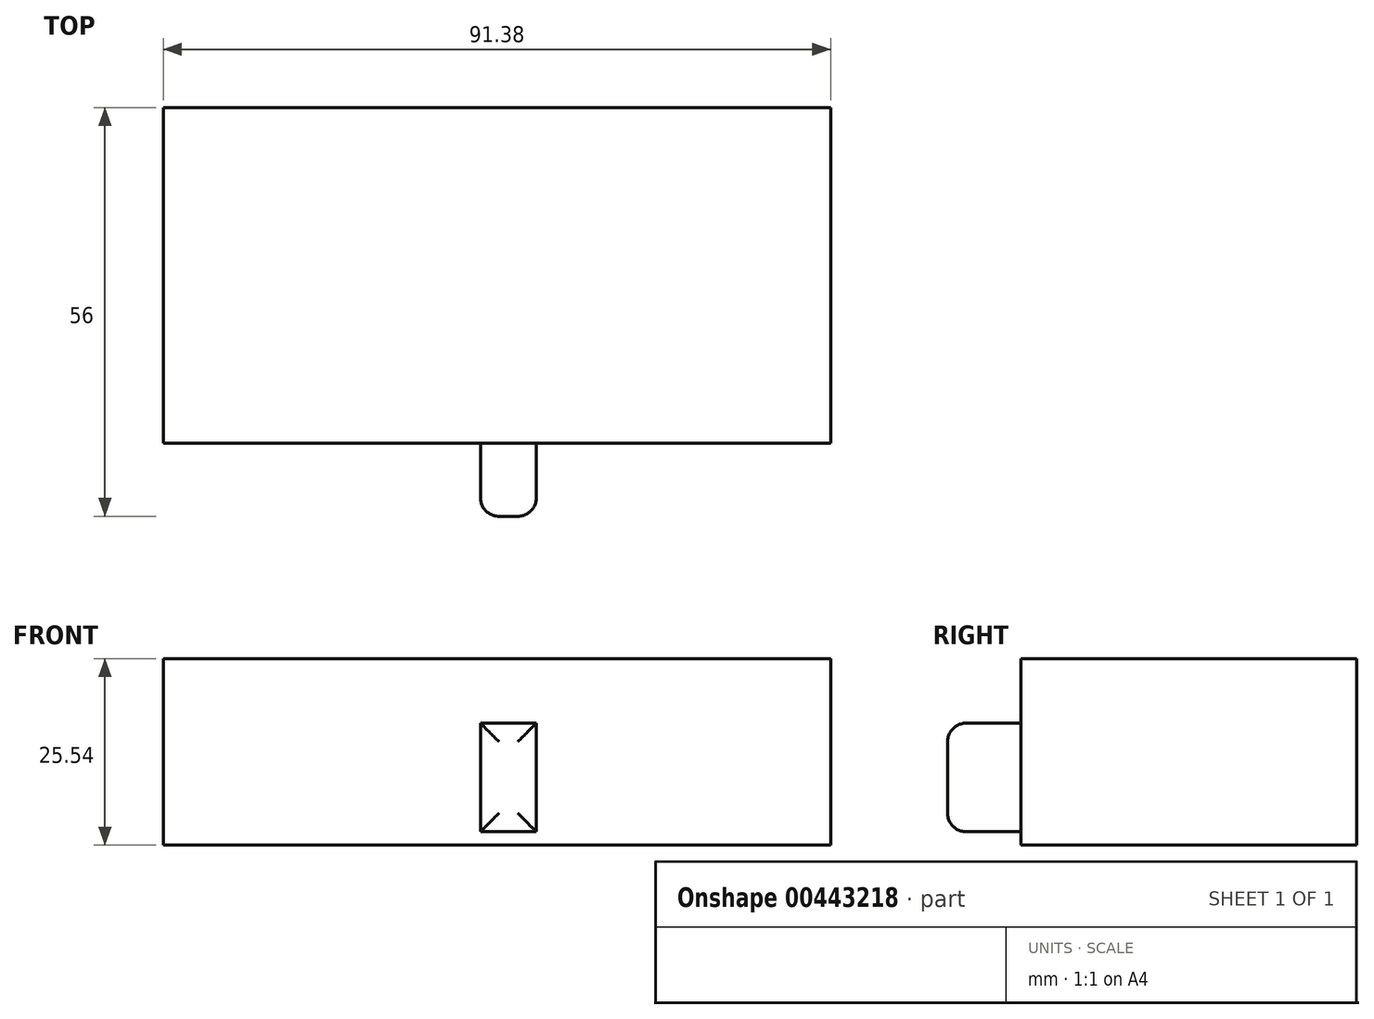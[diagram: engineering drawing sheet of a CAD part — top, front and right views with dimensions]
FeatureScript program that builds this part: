
annotation { "Feature Type Name" : "Feature", "Feature Type Description" : "" }
export const myFeature = defineFeature(function(context is Context, id is Id, definition is map)
    precondition{}
    {
        {
            var Q0;
            Q0=qCreatedBy(makeId("Right.planeOp"),FACE);
            var sketch = newSketch(context, id + "F0", { "sketchPlane" : qUnion([Q0])});
            skLineSegment(sketch, "E0.bottom", {"start": v(-26.5, 0) * mm, "end": v(19.44, 0) * mm});
            skLineSegment(sketch, "E0.top", {"start": v(-26.5, 25.54) * mm, "end": v(19.44, 25.54) * mm});
            skLineSegment(sketch, "E0.left", {"start": v(-26.5, 0) * mm, "end": v(-26.5, 25.54) * mm});
            skLineSegment(sketch, "E0.right", {"start": v(19.44, 0) * mm, "end": v(19.44, 25.54) * mm});
            skSolve(sketch);
        }
        {
            var Q0;
            Q0=makeQuery(id+"F0.imprint","IMPRINT",FACE,{"disambiguationData":[TD([[makeQuery(id+"F0.imprint","IMPRINT",EDGE,{"derivedFrom":sQuery(id+"F0.wireOp",EDGE,"E0.bottom")}),1.0]])]});
            extrude(context, id + "F1", {"entities" : qUnion([Q0]), "depth" : 91.38 * mm});
        }
        {
            var Q0;
            Q0=makeQuery(id+"F1.opExtrude","SWEPT_FACE",FACE,{"disambiguationData":[OSD([sQuery(id+"F0.wireOp",EDGE,"E0.left")])]});
            var sketch = newSketch(context, id + "F2", { "sketchPlane" : qUnion([Q0])});
            skLineSegment(sketch, "E1.bottom", {"start": v(51.08, 16.7) * mm, "end": v(43.43, 16.7) * mm});
            skLineSegment(sketch, "E1.top", {"start": v(51.08, 1.83) * mm, "end": v(43.43, 1.83) * mm});
            skLineSegment(sketch, "E1.left", {"start": v(51.08, 16.7) * mm, "end": v(51.08, 1.83) * mm});
            skLineSegment(sketch, "E1.right", {"start": v(43.43, 16.7) * mm, "end": v(43.43, 1.83) * mm});
            skPoint(sketch, "E1.middle", {"position": v(47.25, 9.27) * mm});
            skSolve(sketch);
        }
        {
            var Q0;
            Q0=makeQuery(id+"F2.imprint","IMPRINT",FACE,{"disambiguationData":[TD([[makeQuery(id+"F2.imprint","IMPRINT",EDGE,{"derivedFrom":sQuery(id+"F2.wireOp",EDGE,"E1.bottom")}),1.0]])]});
            var Q1;
            Q1=sQuery(id+"F2.wireOp",EDGE,"E1.right");
            var Q2;
            Q2=sQuery(id+"F2.wireOp",EDGE,"E1.bottom");
            var Q3;
            Q3=sQuery(id+"F2.wireOp",EDGE,"E1.left");
            var Q4;
            Q4=sQuery(id+"F2.wireOp",EDGE,"E1.top");
            extrude(context, id + "F3", {"entities" : qUnion([Q0]), "operationType" : NewBodyOperationType.ADD, "surfaceEntities" : qUnion([Q1, Q2, Q3, Q4]), "depth" : 10.05 * mm});
        }
        {
            var Q0;
            Q0=makeQuery(id+"F3.opExtrude","CAP_EDGE",EDGE,{"disambiguationData":[OSD([sQuery(id+"F2.wireOp",EDGE,"E1.right")])],"isStart":false});
            var Q1;
            Q1=makeQuery(id+"F3.opExtrude","CAP_EDGE",EDGE,{"disambiguationData":[OSD([sQuery(id+"F2.wireOp",EDGE,"E1.top")])],"isStart":false});
            var Q2;
            Q2=makeQuery(id+"F3.opExtrude","CAP_EDGE",EDGE,{"disambiguationData":[OSD([sQuery(id+"F2.wireOp",EDGE,"E1.left")])],"isStart":false});
            var Q3;
            Q3=makeQuery(id+"F3.opExtrude","CAP_EDGE",EDGE,{"disambiguationData":[OSD([sQuery(id+"F2.wireOp",EDGE,"E1.bottom")])],"isStart":false});
            fillet(context, id + "F4", {"entities" : qUnion([Q0, Q1, Q2, Q3]), "radius" : 2.54 * mm, "tangentPropagation" : true, "allowEdgeOverflow" : false});
        }
    });
